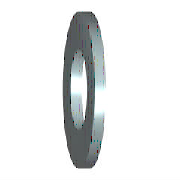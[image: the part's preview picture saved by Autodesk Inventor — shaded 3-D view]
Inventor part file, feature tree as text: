
AUTODESK INVENTOR PART (.ipt)
format: ipt  version: 2024 (Build 280153000, 153)  size: 104,960 bytes
history: native  units: mm (DEFAULTED — no unit token found)
features: other x1, plane x1, sketch x1
ambient origin geometry x7: Origin, YZ Plane, XY Plane, X Axis, Y Axis, Z Axis, Center Point
bodies: Solid1 (feature_tree), Body (feature_tree)
feature tree (3):
  other  "Work Axis1"
  plane  "Work Plane1"
  sketch  "Sketch"  dims[d0=4.3mm d1=9.0mm d2=0.8mm d3=0.0mm d4=0.0mm d5=0.0mm d6=0.0mm d7=0.0mm]
